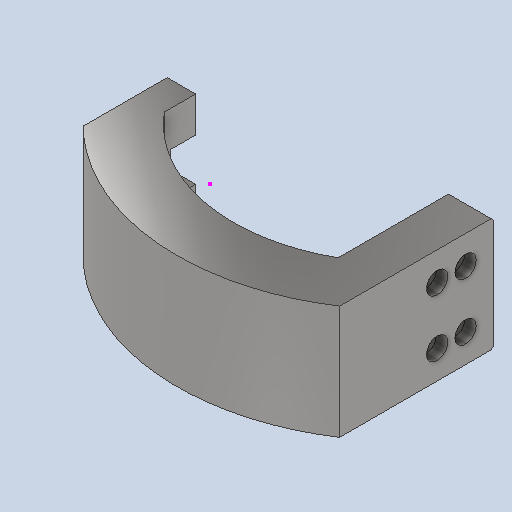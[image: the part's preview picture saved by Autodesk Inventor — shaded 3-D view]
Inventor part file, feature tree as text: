
AUTODESK INVENTOR PART (.ipt)
format: ipt  version: 2023.2 (Build 272271030, 271C)  size: 336,896 bytes
history: native  units: mm
features: sketch x9, plane x5, extrude x3, hole x3, chamfer x2
ambient origin geometry x8: Origin, YZ Plane, XZ Plane, XY Plane, X Axis, Y Axis, Z Axis, Center Point
bodies: Solid1 (feature_tree)
feature tree (22):
  sketch  "Sketch1"  dims[d0=30.0mm d1=25.0mm]
  plane  "Work Plane1"
  plane  "Work Plane5"
  plane  "Work Plane4"
  plane  "Work Plane2"
  sketch  "Sketch7"  dims[d3=320.0mm d4=240.0mm]
  plane  "Work Plane3"
  extrude  "Extrusion4"  Depth=25.0mm
  extrude  "Extrusion5"  Depth=240.0mm
  extrude  "Extrusion6"  Depth=25.0mm TaperAngle=0.0deg
  sketch  "Sketch11"  dims[d80=48.0mm d81=30.0mm d82=0.0mm d83=25.0mm d84=0.0mm]
  sketch  "Sketch14"  dims[d129=2.0mm d130=2.0mm d131=45.0deg d132=2.0mm d133=2.0mm d134=45.0deg]
  chamfer  "Chamfer7"  Distance=30.0mm
  chamfer  "Chamfer8"  Distance=25.0mm
  hole  "Hole7"  [1 undecoded]
  hole  "Hole8"  [1 undecoded]
  hole  "Hole9"  [1 undecoded]
  sketch  "Sketch9"  dims[d6=20.0mm d77=25.0mm d78=0.0mm]
  sketch  "Sketch10"  dims[d79=20.0mm]
  sketch  "Sketch16"  dims[d137=30.0mm d138=15.0mm]
  sketch  "Sketch17"  dims[d139=15.0mm d140=15.0mm]
  sketch  "Sketch18"  dims[d141=15.0mm d142=20.0mm d143=20.0mm d144=20.0mm d145=20.0mm d146=20.0mm d147=20.0mm d148=20.0mm d149=20.0mm d150=15.0mm d151=6.0mm d152=4.0mm d153=2.0mm d154=90.0deg d155=8.0mm d156=0.0mm d157=8.4mm d158=8.4mm d159=8.4mm d160=8.4mm d161=40.0mm d162=20.0mm d163=40.0mm d164=20.0mm d165=8.4mm d166=6.0mm d167=4.0mm d168=2.0mm d169=90.0deg d170=50.0mm d171=0.0mm d172=8.0mm d173=8.0mm d174=15.0mm d175=15.0mm d176=17.5mm d177=17.5mm d178=45.0mm d179=8.0mm d180=6.0mm d181=4.0mm d182=2.0mm d183=90.0deg d184=12.0mm d185=20.594885mm]
note: 3 required parameter values undecoded (feature->parameter linkage not recoverable at this tier; creation-order binding heuristic only, values carry confidence <= 0.55)
